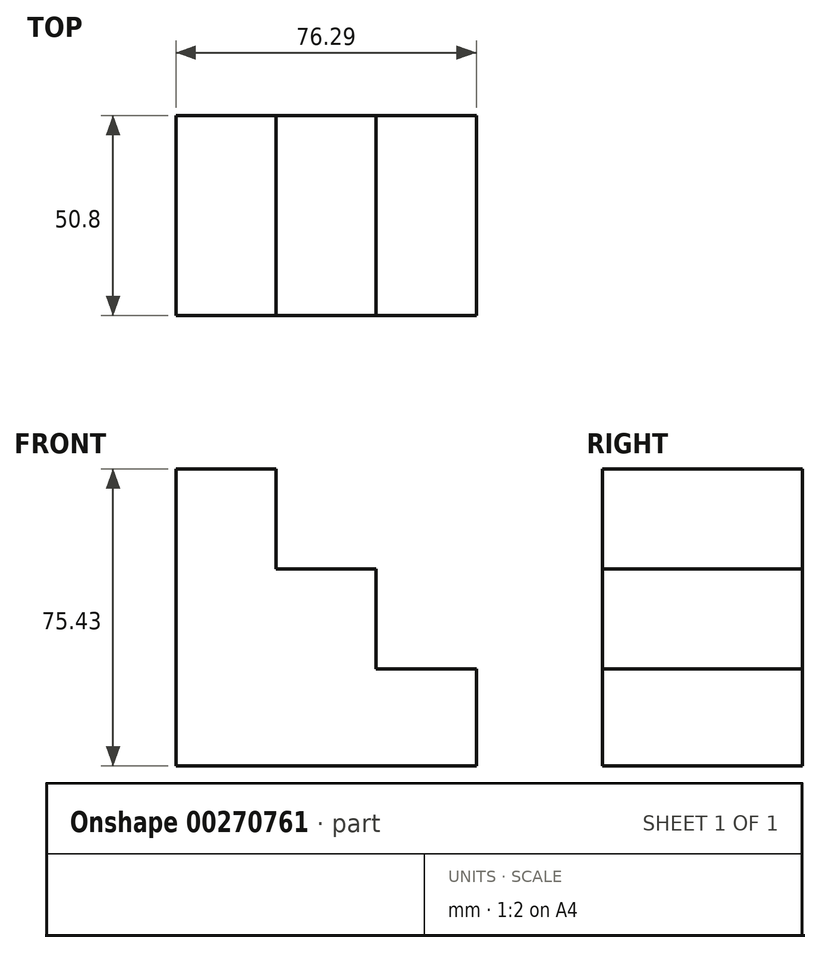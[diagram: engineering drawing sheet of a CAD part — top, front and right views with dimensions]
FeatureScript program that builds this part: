
annotation { "Feature Type Name" : "Feature", "Feature Type Description" : "" }
export const myFeature = defineFeature(function(context is Context, id is Id, definition is map)
    precondition{}
    {
        {
            var Q0;
            Q0=qCreatedBy(makeId("Front.planeOp"),FACE);
            var sketch = newSketch(context, id + "F0", { "sketchPlane" : qUnion([Q0])});
            skLineSegment(sketch, "E0", {"start": v(0, 0) * mm, "end": v(-76.29, 0) * mm});
            skLineSegment(sketch, "E1", {"start": v(-76.29, 0) * mm, "end": v(-76.29, 75.43) * mm});
            skLineSegment(sketch, "E2", {"start": v(-76.29, 75.43) * mm, "end": v(-50.89, 75.43) * mm});
            skLineSegment(sketch, "E3", {"start": v(-50.89, 75.43) * mm, "end": v(-50.89, 50.03) * mm});
            skLineSegment(sketch, "E4", {"start": v(-50.89, 50.03) * mm, "end": v(-25.49, 50.03) * mm});
            skLineSegment(sketch, "E5", {"start": v(-25.49, 50.03) * mm, "end": v(-25.49, 24.63) * mm});
            skLineSegment(sketch, "E6", {"start": v(-25.49, 24.63) * mm, "end": v(0, 24.63) * mm});
            skLineSegment(sketch, "E7", {"start": v(0, 24.63) * mm, "end": v(0, 0) * mm});
            skSolve(sketch);
        }
        {
            var Q0;
            Q0 = qSketchRegion(id + "F0", true);
            extrude(context, id + "F1", {"entities" : qUnion([Q0]), "depth" : 50.8 * mm});
        }
    });
